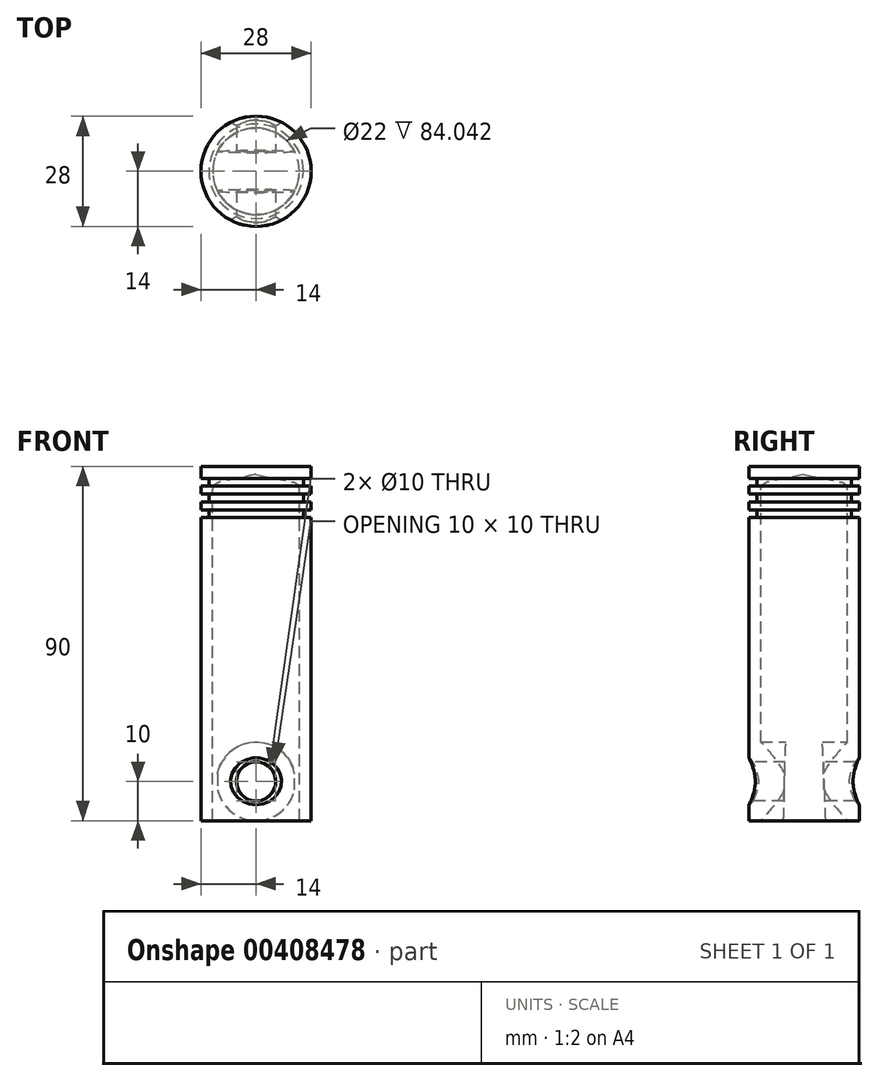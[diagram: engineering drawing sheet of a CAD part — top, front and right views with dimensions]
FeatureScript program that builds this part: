
annotation { "Feature Type Name" : "Feature", "Feature Type Description" : "" }
export const myFeature = defineFeature(function(context is Context, id is Id, definition is map)
    precondition{}
    {
        {
            var Q0;
            Q0=qCreatedBy(makeId("Top.planeOp"),FACE);
            var sketch = newSketch(context, id + "F0", { "sketchPlane" : qUnion([Q0])});
            skCircle(sketch, "E0", {"center": v(0, 0) * mm, "radius": 14 * mm});
            skSolve(sketch);
        }
        {
            var Q0;
            Q0=makeQuery(id+"F0.imprint","IMPRINT",FACE,{"disambiguationData":[TD([[makeQuery(id+"F0.imprint","IMPRINT",EDGE,{"derivedFrom":sQuery(id+"F0.wireOp",EDGE,"E0")}),1.0]])]});
            extrude(context, id + "F1", {"entities" : qUnion([Q0]), "depth" : 90 * mm});
        }
        {
            var Q0;
            Q0=qCreatedBy(makeId("Right.planeOp"),FACE);
            var sketch = newSketch(context, id + "F2", { "sketchPlane" : qUnion([Q0])});
            skLineSegment(sketch, "E1", {"start": v(0, 0) * mm, "end": v(0, 88) * mm});
            skLineSegment(sketch, "E2", {"start": v(0, 88) * mm, "end": v(-9.42, 86) * mm});
            skLineSegment(sketch, "E3", {"start": v(-11, 84.04) * mm, "end": v(-11, 0) * mm});
            skLineSegment(sketch, "E4", {"start": v(-11, 0) * mm, "end": v(0, 0) * mm});
            skPoint(sketch, "E5.visualSharp", {"position": v(-11, 85.66) * mm});
            skArc(sketch, "E5.filletArc", {"start": v(-9.42, 86) * mm, "mid": v(-10.55, 85.3) * mm, "end": v(-11, 84.04) * mm});
            skSolve(sketch);
        }
        {
            var Q0;
            Q0 = qSketchRegion(id + "F2", true);
            var Q1;
            Q1=sQuery(id+"F2.wireOp",EDGE,"E1");
            revolve(context, id + "F3", {"operationType" : NewBodyOperationType.REMOVE, "entities" : qUnion([Q0]), "axis" : qUnion([Q1]), "revolveType" : RevolveType.FULL, "oppositeDirection" : true});
        }
        {
            var Q0;
            Q0=qCreatedBy(makeId("Front.planeOp"),FACE);
            var sketch = newSketch(context, id + "F4", { "sketchPlane" : qUnion([Q0])});
            skCircle(sketch, "E6", {"center": v(0, 10) * mm, "radius": 10 * mm});
            skSolve(sketch);
        }
        {
            var Q0;
            Q0=makeQuery(id+"F4.imprint","IMPRINT",FACE,{"disambiguationData":[TD([[makeQuery(id+"F4.imprint","IMPRINT",EDGE,{"derivedFrom":sQuery(id+"F4.wireOp",EDGE,"E6")}),1.0]])]});
            var Q1;
            Q1=makeQuery(id+"F3.boolean.opBoolean","COPY",FACE,{"derivedFrom":makeQuery(id+"F3.opRevolve","SWEPT_FACE",FACE,{"disambiguationData":[OSD([sQuery(id+"F2.wireOp",EDGE,"E3")])]})});
            var Q2;
            Q2=makeQuery(id+"F3.boolean.opBoolean","COPY",FACE,{"derivedFrom":makeQuery(id+"F3.opRevolve","SWEPT_FACE",FACE,{"disambiguationData":[OSD([sQuery(id+"F2.wireOp",EDGE,"E3")])]})});
            extrude(context, id + "F5", {"entities" : qUnion([Q0]), "operationType" : NewBodyOperationType.ADD, "endBound" : BoundingType.UP_TO_SURFACE, "endBoundEntityFace" : qUnion([Q1]), "depth" : 25 * mm, "hasSecondDirection" : true, "secondDirectionBound" : SecondDirectionBoundingType.UP_TO_SURFACE, "secondDirectionOppositeDirection" : true, "secondDirectionBoundEntityFace" : qUnion([Q2]), "secondDirectionDepth" : 25 * mm});
        }
        {
            var Q0;
            Q0=qCreatedBy(makeId("Right.planeOp"),FACE);
            var sketch = newSketch(context, id + "F6", { "sketchPlane" : qUnion([Q0])});
            skLineSegment(sketch, "E7", {"start": v(0, 0) * mm, "end": v(0, 42.66) * mm, "construction": true});
            skLineSegment(sketch, "E8", {"start": v(0, 20) * mm, "end": v(-4.66, 20) * mm});
            skLineSegment(sketch, "E9", {"start": v(-4.66, 20) * mm, "end": v(-5.36, 0) * mm});
            skLineSegment(sketch, "E10", {"start": v(-5.36, 0) * mm, "end": v(0, 0) * mm});
            skLineSegment(sketch, "E11.MirrorCS", {"start": v(0, 20) * mm, "end": v(4.66, 20) * mm});
            skLineSegment(sketch, "E12.MirrorCS", {"start": v(4.66, 20) * mm, "end": v(5.36, 0) * mm});
            skLineSegment(sketch, "E13.MirrorCS", {"start": v(5.36, 0) * mm, "end": v(0, 0) * mm});
            skSolve(sketch);
        }
        {
            var Q0;
            Q0 = qSketchRegion(id + "F6", true);
            var Q1;
            Q1=makeQuery(id+"F3.boolean.opBoolean","COPY",FACE,{"derivedFrom":makeQuery(id+"F3.opRevolve","SWEPT_FACE",FACE,{"disambiguationData":[OSD([sQuery(id+"F2.wireOp",EDGE,"E3")])]})});
            var Q2;
            Q2=makeQuery(id+"F3.boolean.opBoolean","COPY",FACE,{"derivedFrom":makeQuery(id+"F3.opRevolve","SWEPT_FACE",FACE,{"disambiguationData":[OSD([sQuery(id+"F2.wireOp",EDGE,"E3")])]})});
            extrude(context, id + "F7", {"entities" : qUnion([Q0]), "operationType" : NewBodyOperationType.REMOVE, "endBound" : BoundingType.UP_TO_SURFACE, "oppositeDirection" : true, "endBoundEntityFace" : qUnion([Q1]), "depth" : 18 * mm, "hasSecondDirection" : true, "secondDirectionBound" : SecondDirectionBoundingType.UP_TO_SURFACE, "secondDirectionOppositeDirection" : false, "secondDirectionBoundEntityFace" : qUnion([Q2]), "secondDirectionDepth" : 25 * mm});
        }
        {
            var Q0;
            Q0=qCreatedBy(makeId("Front.planeOp"),FACE);
            var sketch = newSketch(context, id + "F8", { "sketchPlane" : qUnion([Q0])});
            skCircle(sketch, "E14", {"center": v(0, 10) * mm, "radius": 5 * mm});
            skSolve(sketch);
        }
        {
            var Q0;
            Q0 = qSketchRegion(id + "F8", true);
            extrude(context, id + "F9", {"entities" : qUnion([Q0]), "operationType" : NewBodyOperationType.REMOVE, "endBound" : BoundingType.SYMMETRIC, "oppositeDirection" : true, "depth" : 40 * mm});
        }
        {
            var Q0;
            Q0=makeQuery(id+"F9.boolean.opBoolean","INTERSECT",EDGE,{"disambiguationData":[OD(0.0)],"derivedFrom":[makeQuery(id+"F1.opExtrude","SWEPT_FACE",FACE,{"disambiguationData":[OSD([sQuery(id+"F0.wireOp",EDGE,"E0")])]}),makeQuery(id+"F9.opExtrude","SWEPT_FACE",FACE,{"disambiguationData":[OSD([sQuery(id+"F8.wireOp",EDGE,"E14")])]})]});
            var Q1;
            Q1=makeQuery(id+"F9.boolean.opBoolean","INTERSECT",EDGE,{"disambiguationData":[OD(1.0)],"derivedFrom":[makeQuery(id+"F1.opExtrude","SWEPT_FACE",FACE,{"disambiguationData":[OSD([sQuery(id+"F0.wireOp",EDGE,"E0")])]}),makeQuery(id+"F9.opExtrude","SWEPT_FACE",FACE,{"disambiguationData":[OSD([sQuery(id+"F8.wireOp",EDGE,"E14")])]})]});
            chamfer(context, id + "F10", {"entities" : qUnion([Q0, Q1]), "chamferType" : ChamferType.OFFSET_ANGLE, "width" : 1 * mm, "oppositeDirection" : false, "angle" : 45 * degree, "tangentPropagation" : true});
        }
        {
            var Q0;
            Q0=qCreatedBy(makeId("Right.planeOp"),FACE);
            var sketch = newSketch(context, id + "F11", { "sketchPlane" : qUnion([Q0])});
            skLineSegment(sketch, "E15.bottom", {"start": v(-14, 87) * mm, "end": v(-12, 87) * mm});
            skLineSegment(sketch, "E15.top", {"start": v(-14, 85) * mm, "end": v(-12, 85) * mm});
            skLineSegment(sketch, "E15.left", {"start": v(-14, 87) * mm, "end": v(-14, 85) * mm});
            skLineSegment(sketch, "E15.right", {"start": v(-12, 87) * mm, "end": v(-12, 85) * mm});
            skLineSegment(sketch, "E16.bottom", {"start": v(-14, 83) * mm, "end": v(-12, 83) * mm});
            skLineSegment(sketch, "E16.top", {"start": v(-14, 81) * mm, "end": v(-12, 81) * mm});
            skLineSegment(sketch, "E16.left", {"start": v(-14, 83) * mm, "end": v(-14, 81) * mm});
            skLineSegment(sketch, "E16.right", {"start": v(-12, 83) * mm, "end": v(-12, 81) * mm});
            skLineSegment(sketch, "E17.bottom", {"start": v(-14, 79) * mm, "end": v(-12, 79) * mm});
            skLineSegment(sketch, "E17.top", {"start": v(-14, 77) * mm, "end": v(-12, 77) * mm});
            skLineSegment(sketch, "E17.left", {"start": v(-14, 79) * mm, "end": v(-14, 77) * mm});
            skLineSegment(sketch, "E17.right", {"start": v(-12, 79) * mm, "end": v(-12, 77) * mm});
            skSolve(sketch);
        }
        {
            var Q0;
            Q0 = qSketchRegion(id + "F11", true);
            var Q1;
            Q1=makeQuery(id+"F1.opExtrude","CAP_EDGE",EDGE,{"disambiguationData":[OSD([sQuery(id+"F0.wireOp",EDGE,"E0")])],"isStart":false});
            revolve(context, id + "F12", {"operationType" : NewBodyOperationType.REMOVE, "entities" : qUnion([Q0]), "axis" : qUnion([Q1]), "revolveType" : RevolveType.FULL, "oppositeDirection" : true});
        }
    });
